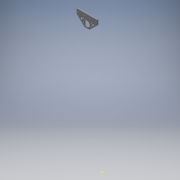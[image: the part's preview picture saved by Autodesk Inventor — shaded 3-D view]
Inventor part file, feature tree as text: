
AUTODESK INVENTOR PART (.ipt)
format: ipt  version: 2017 (Build 210142000, 142)  size: 768,000 bytes
history: native  units: mm
features: sketch x4, extrude x3, projected_geometry x1
ambient origin geometry x8: Origin, YZ Plane, XZ Plane, XY Plane, X Axis, Y Axis, Z Axis, Center Point
bodies: Solid1 (feature_tree)
feature tree (8):
  extrude  "Extrusion1"  Depth=6.0mm TaperAngle=0.0deg
  extrude  "Extrusion2"  Depth=12.0mm
  sketch  "Sketch3"  dims[d6=3.2mm d7=3.2mm]
  sketch  "Sketch4"  dims[d8=3.2mm d9=3.2mm d10=3.2mm d11=3.2mm d12=5.2mm d13=5.2mm d14=5.2mm d15=6.0mm d16=0.0mm]
  extrude  "Extrusion3"  Depth=3.2mm
  sketch  "Sketch1"  dims[d0=6.0mm d1=0.0mm d2=6.0mm d3=0.0mm]
  sketch  "Sketch2"  dims[d4=12.0mm d5=12.0mm]
  projected_geometry  "Projected Loop1"
